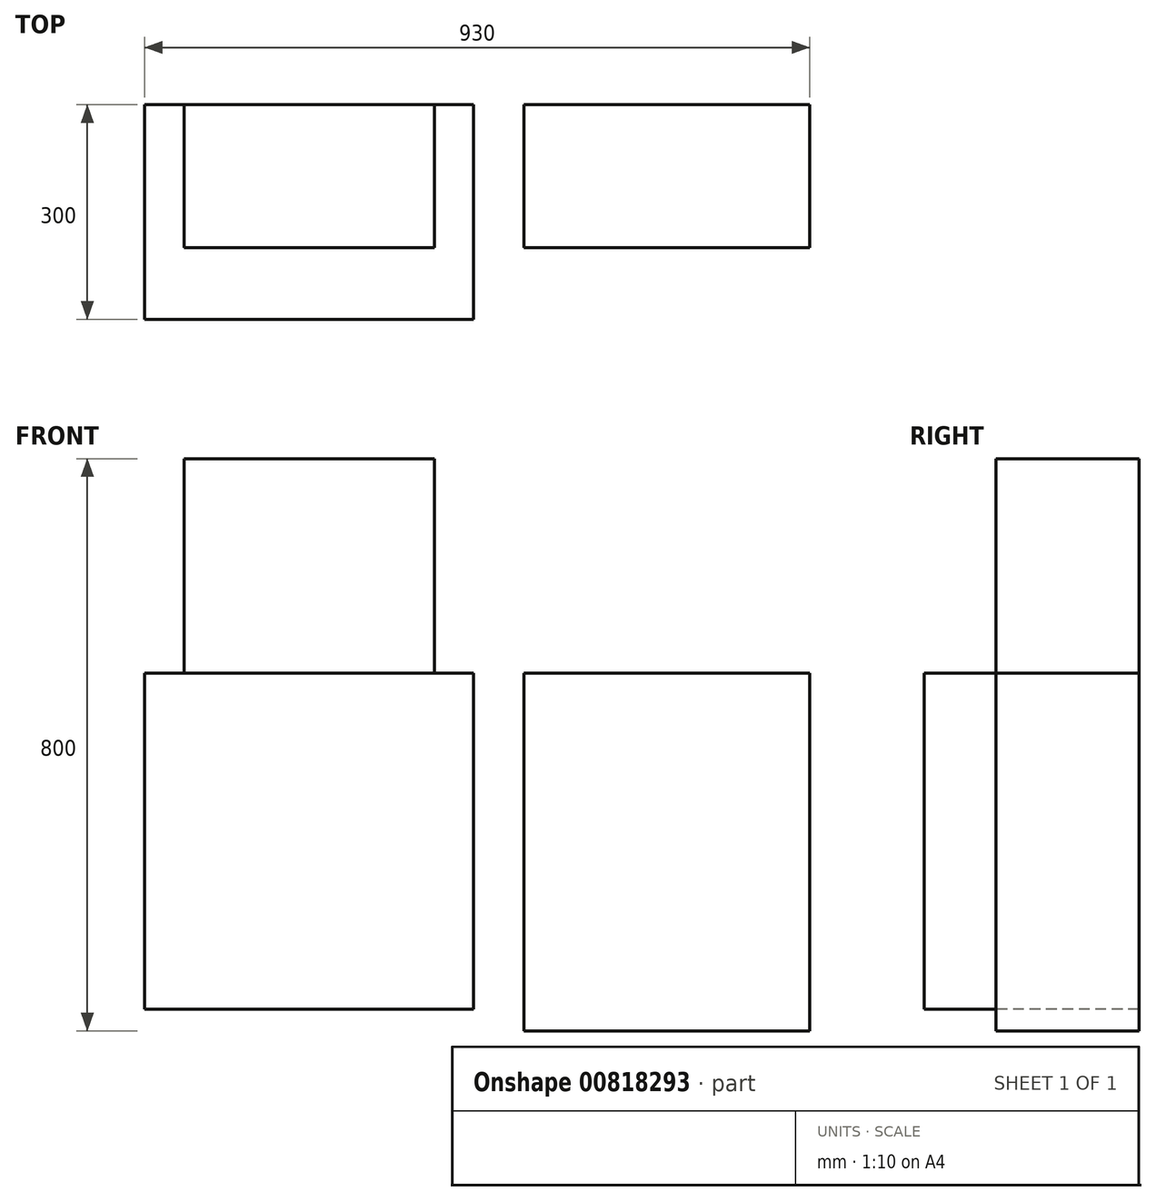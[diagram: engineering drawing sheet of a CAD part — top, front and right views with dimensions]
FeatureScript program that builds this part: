
annotation { "Feature Type Name" : "Feature", "Feature Type Description" : "" }
export const myFeature = defineFeature(function(context is Context, id is Id, definition is map)
    precondition{}
    {
        {
            var Q0;
            Q0=qCreatedBy(makeId("Front.planeOp"),FACE);
            var sketch = newSketch(context, id + "F0", { "sketchPlane" : qUnion([Q0])});
            skLineSegment(sketch, "E0.bottom", {"start": v(0, 0) * mm, "end": v(-460, 0) * mm});
            skLineSegment(sketch, "E0.top", {"start": v(0, 470) * mm, "end": v(-460, 470) * mm});
            skLineSegment(sketch, "E0.left", {"start": v(0, 0) * mm, "end": v(0, 470) * mm});
            skLineSegment(sketch, "E0.right", {"start": v(-460, 0) * mm, "end": v(-460, 470) * mm});
            skSolve(sketch);
        }
        {
            var Q0;
            Q0 = qSketchRegion(id + "F0", true);
            extrude(context, id + "F1", {"entities" : qUnion([Q0]), "oppositeDirection" : true, "depth" : 300 * mm, "offsetDistance" : 25 * mm});
        }
        {
            var Q0;
            Q0=makeQuery(id+"F1.opExtrude","CAP_FACE",FACE,{"disambiguationData":[OSD([sQuery(id+"F0.wireOp",EDGE,"E0.bottom"),sQuery(id+"F0.wireOp",EDGE,"E0.top"),sQuery(id+"F0.wireOp",EDGE,"E0.left"),sQuery(id+"F0.wireOp",EDGE,"E0.right")])],"isStart":false});
            var sketch = newSketch(context, id + "F2", { "sketchPlane" : qUnion([Q0])});
            skLineSegment(sketch, "E1.0", {"start": v(0, 470) * mm, "end": v(460, 470) * mm, "construction": true});
            skLineSegment(sketch, "E2", {"start": v(230, 470) * mm, "end": v(55, 470) * mm});
            skLineSegment(sketch, "E3", {"start": v(55, 470) * mm, "end": v(55, 770) * mm});
            skLineSegment(sketch, "E4", {"start": v(55, 770) * mm, "end": v(405, 770) * mm});
            skLineSegment(sketch, "E5", {"start": v(405, 770) * mm, "end": v(405, 470) * mm});
            skLineSegment(sketch, "E6", {"start": v(405, 470) * mm, "end": v(230, 470) * mm});
            skLineSegment(sketch, "E7", {"start": v(0, 470) * mm, "end": v(-70, 470) * mm, "construction": true});
            skLineSegment(sketch, "E8.bottom", {"start": v(-70, 470) * mm, "end": v(-470, 470) * mm});
            skLineSegment(sketch, "E8.top", {"start": v(-70, -30) * mm, "end": v(-470, -30) * mm});
            skLineSegment(sketch, "E8.left", {"start": v(-70, 470) * mm, "end": v(-70, -30) * mm});
            skLineSegment(sketch, "E8.right", {"start": v(-470, 470) * mm, "end": v(-470, -30) * mm});
            skSolve(sketch);
        }
        {
            var Q0;
            Q0 = qSketchRegion(id + "F2", true);
            extrude(context, id + "F3", {"entities" : qUnion([Q0]), "operationType" : NewBodyOperationType.ADD, "oppositeDirection" : true, "depth" : 200 * mm, "offsetDistance" : 25 * mm});
        }
    });
